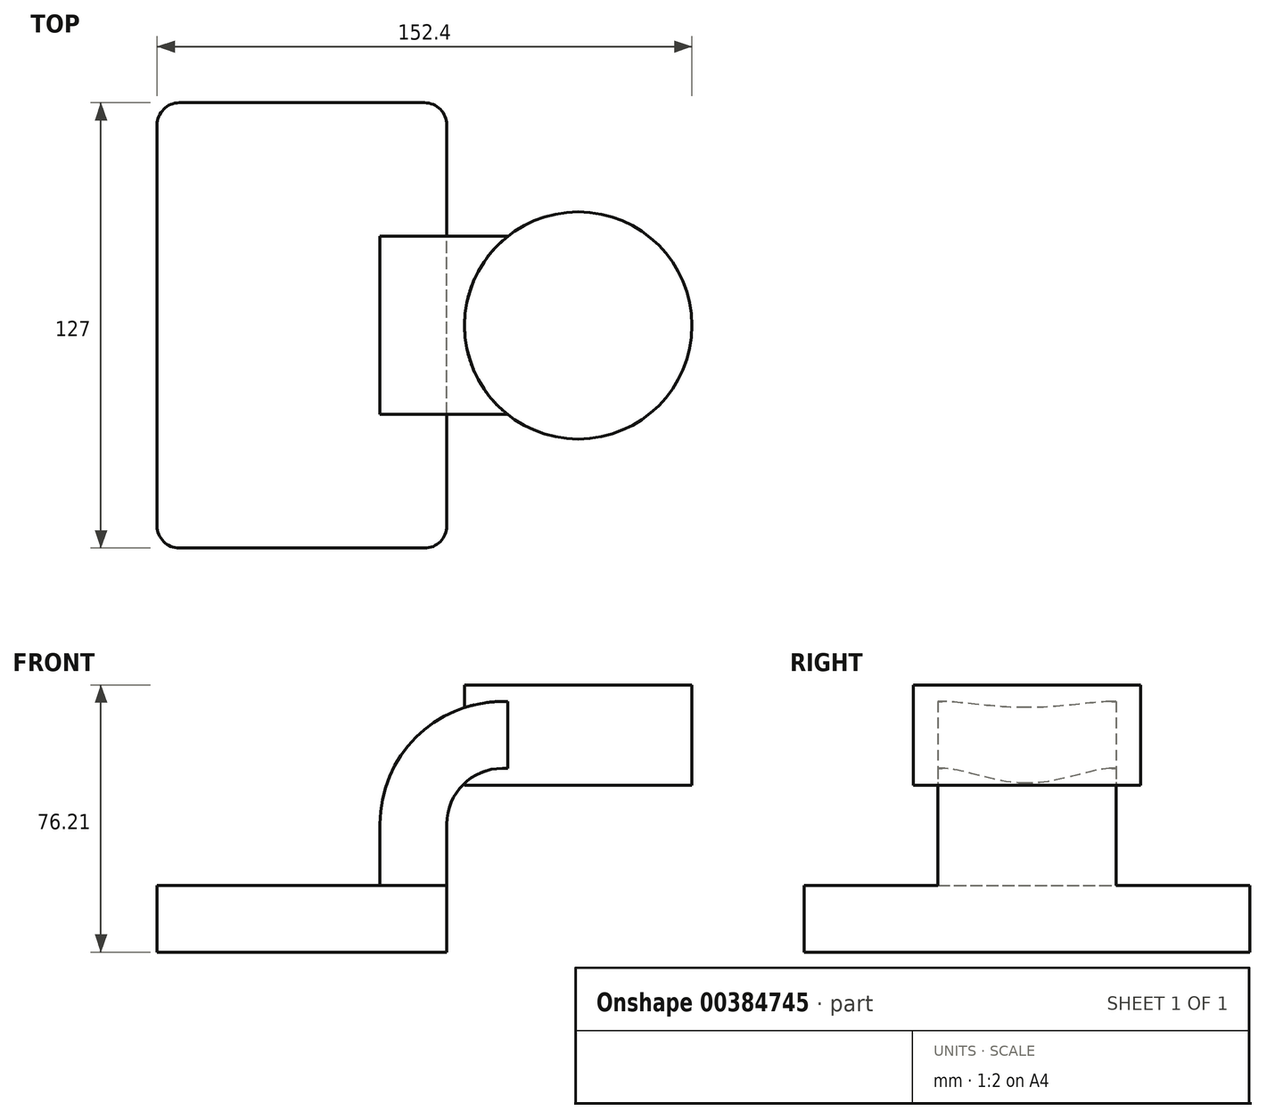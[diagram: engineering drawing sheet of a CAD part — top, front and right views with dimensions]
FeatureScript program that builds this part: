
annotation { "Feature Type Name" : "Feature", "Feature Type Description" : "" }
export const myFeature = defineFeature(function(context is Context, id is Id, definition is map)
    precondition{}
    {
        {
            var Q0;
            Q0=qCreatedBy(makeId("Front.planeOp"),FACE);
            var sketch = newSketch(context, id + "F0", { "sketchPlane" : qUnion([Q0])});
            skLineSegment(sketch, "E0.bottom", {"start": v(41.27, 9.53) * mm, "end": v(-41.28, 9.53) * mm});
            skLineSegment(sketch, "E0.top", {"start": v(41.28, -9.52) * mm, "end": v(-41.27, -9.52) * mm});
            skLineSegment(sketch, "E0.left", {"start": v(41.28, 9.53) * mm, "end": v(41.28, -9.52) * mm});
            skLineSegment(sketch, "E0.right", {"start": v(-41.28, 9.53) * mm, "end": v(-41.27, -9.52) * mm});
            skPoint(sketch, "E0.middle", {"position": v(0, 0) * mm});
            skLineSegment(sketch, "E1.bottom", {"start": v(60.32, 66.68) * mm, "end": v(111.12, 66.68) * mm});
            skLineSegment(sketch, "E1.top", {"start": v(60.33, 38.1) * mm, "end": v(111.12, 38.1) * mm});
            skLineSegment(sketch, "E1.left", {"start": v(60.32, 66.68) * mm, "end": v(60.33, 38.1) * mm});
            skLineSegment(sketch, "E1.right", {"start": v(111.12, 66.68) * mm, "end": v(111.12, 38.1) * mm});
            skPoint(sketch, "E1.middle", {"position": v(85.72, 52.39) * mm});
            skLineSegment(sketch, "E2", {"start": v(41.27, 9.53) * mm, "end": v(41.27, 27) * mm});
            skArc(sketch, "E3", {"start": v(41.27, 27) * mm, "mid": v(45.92, 38.23) * mm, "end": v(57.15, 42.88) * mm});
            skLineSegment(sketch, "E4", {"start": v(57.15, 42.88) * mm, "end": v(78.73, 42.88) * mm});
            skLineSegment(sketch, "E5.0", {"start": v(47.62, 9.53) * mm, "end": v(47.62, 27) * mm});
            skLineSegment(sketch, "E6.0", {"start": v(57.15, 61.93) * mm, "end": v(78.73, 61.93) * mm});
            skArc(sketch, "E6.1", {"start": v(22.23, 27) * mm, "mid": v(32.45, 51.7) * mm, "end": v(57.15, 61.93) * mm});
            skLineSegment(sketch, "E6.2", {"start": v(22.22, 9.53) * mm, "end": v(22.22, 27) * mm});
            skLineSegment(sketch, "E7", {"start": v(78.73, 38.1) * mm, "end": v(78.73, 66.68) * mm});
            skPoint(sketch, "E7.startSnap0", {"position": v(85.73, 38.1) * mm});
            skFitSpline(sketch, "E8", {"points": [v(-41.27, 9.52) * mm, v(57.15, 61.93) * mm], "startDerivative": vector(1.93, 108.31) * mm, "endDerivative": vector(122.12, -6.43) * mm});
            skSolve(sketch);
        }
        {
            var Q0;
            Q0=makeQuery(id+"F0.imprint","IMPRINT",FACE,{"disambiguationData":[TD([[makeQuery(id+"F0.imprint","IMPRINT",EDGE,{"derivedFrom":sQuery(id+"F0.wireOp",EDGE,"E0.top")}),-1.0]])]});
            extrude(context, id + "F1", {"entities" : qUnion([Q0]), "depth" : 127 * mm, "symmetric" : true});
        }
        {
            var Q0;
            {var subQ1=sQuery(id+"F0.wireOp",EDGE,"E2");Q0=makeQuery(id+"F0.imprint","IMPRINT",FACE,{"disambiguationData":[TD([[makeQuery(id+"F0.imprint","IMPRINT",EDGE,{"derivedFrom":subQ1}),1.0]])]});}
            var Q1;
            {var subQ0=sQuery(id+"F0.wireOp",EDGE,"E6.0");var subQ1=sQuery(id+"F0.wireOp",EDGE,"E1.left");var subQ2=makeQuery(id+"F0.imprint","INTERSECT",VERTEX,{"derivedFrom":[subQ1,subQ0]});Q1=makeQuery(id+"F0.imprint","IMPRINT",FACE,{"disambiguationData":[TD([[makeQuery(id+"F0.imprint","IMPRINT",EDGE,{"disambiguationData":[TD([[subQ2,-1.0]])],"derivedFrom":subQ1}),1.0]])]});}
            extrude(context, id + "F2", {"entities" : qUnion([Q0, Q1]), "operationType" : NewBodyOperationType.ADD, "depth" : 50.8 * mm, "symmetric" : true});
        }
        {
            var Q0;
            Q0=makeQuery(id+"F0.imprint","IMPRINT",FACE,{"disambiguationData":[TD([[makeQuery(id+"F0.imprint","IMPRINT",EDGE,{"derivedFrom":sQuery(id+"F0.wireOp",EDGE,"E6.1")}),1.0]])]});
            extrude(context, id + "F3", {"entities" : qUnion([Q0]), "operationType" : NewBodyOperationType.ADD, "depth" : 15.88 * mm, "symmetric" : true});
        }
        {
            var Q0;
            {var subQ0=sQuery(id+"F0.wireOp",EDGE,"E1.right");Q0=makeQuery(id+"F0.imprint","IMPRINT",FACE,{"disambiguationData":[TD([[makeQuery(id+"F0.imprint","IMPRINT",EDGE,{"derivedFrom":subQ0}),-1.0]])]});}
            var Q1;
            Q1=sQuery(id+"F0.wireOp",EDGE,"E7");
            revolve(context, id + "F4", {"operationType" : NewBodyOperationType.ADD, "entities" : qUnion([Q0]), "axis" : qUnion([Q1]), "revolveType" : RevolveType.FULL});
        }
        {
            var Q0;
            Q0=makeQuery(id+"F1.opExtrude","CAP_EDGE",EDGE,{"disambiguationData":[OSD([sQuery(id+"F0.wireOp",EDGE,"E0.left")])],"isStart":false});
            var Q1;
            Q1=makeQuery(id+"F1.opExtrude","CAP_EDGE",EDGE,{"disambiguationData":[OSD([sQuery(id+"F0.wireOp",EDGE,"E0.right")])],"isStart":false});
            var Q2;
            Q2=makeQuery(id+"F1.opExtrude","CAP_EDGE",EDGE,{"disambiguationData":[OSD([sQuery(id+"F0.wireOp",EDGE,"E0.left")])],"isStart":true});
            var Q3;
            Q3=makeQuery(id+"F1.opExtrude","CAP_EDGE",EDGE,{"disambiguationData":[OSD([sQuery(id+"F0.wireOp",EDGE,"E0.right")])],"isStart":true});
            fillet(context, id + "F5", {"entities" : qUnion([Q0, Q1, Q2, Q3]), "radius" : 6.35 * mm, "tangentPropagation" : true, "allowEdgeOverflow" : false});
        }
    });
